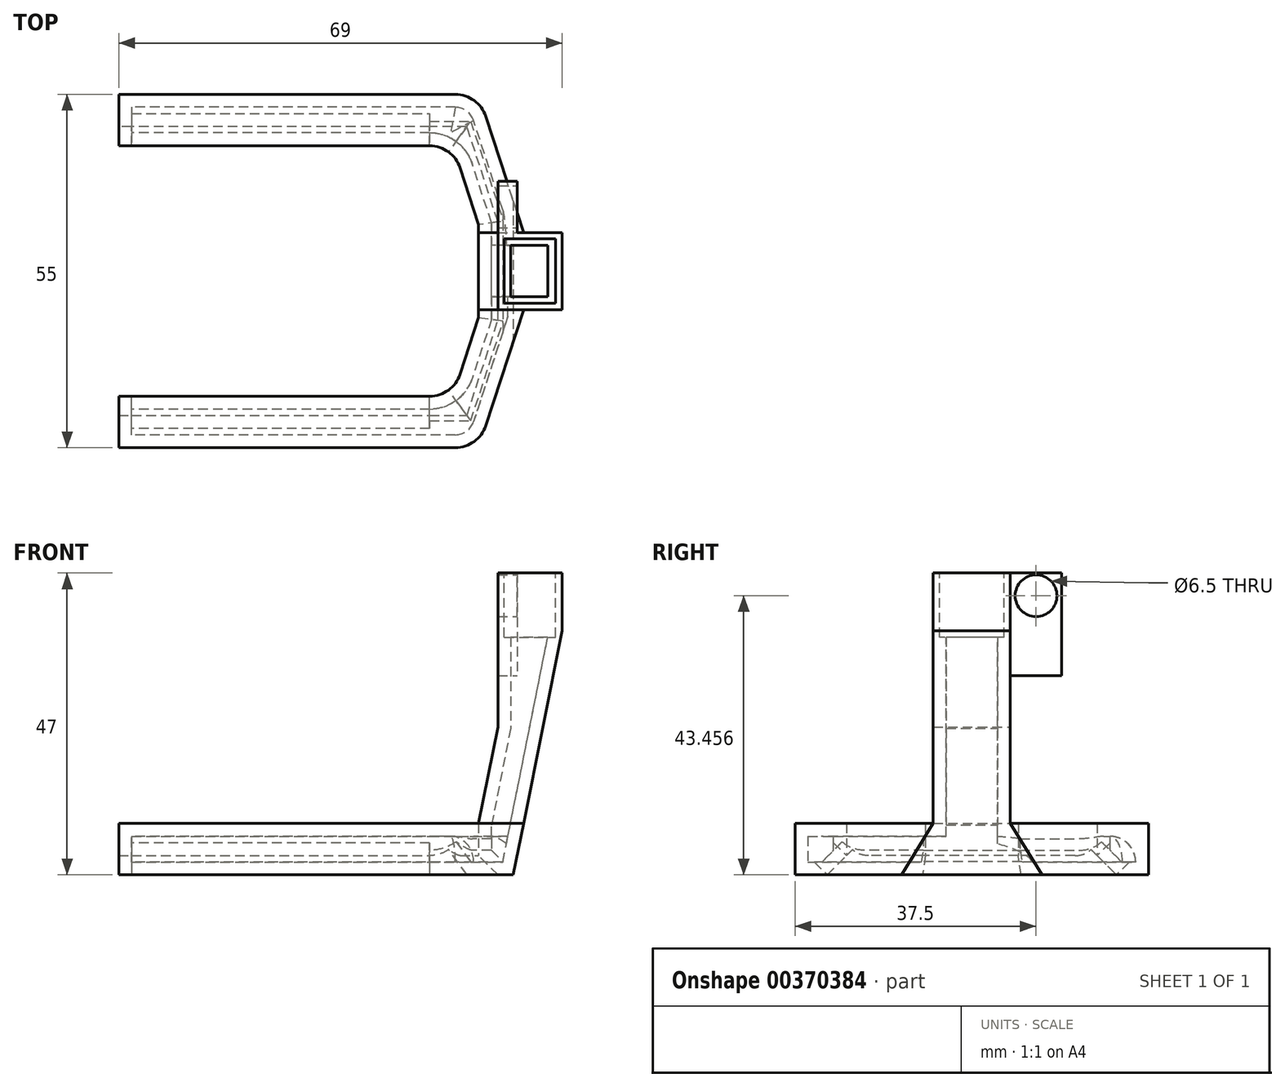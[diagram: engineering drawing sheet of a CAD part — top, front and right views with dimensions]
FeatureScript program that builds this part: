
annotation { "Feature Type Name" : "Feature", "Feature Type Description" : "" }
export const myFeature = defineFeature(function(context is Context, id is Id, definition is map)
    precondition{}
    {
        {
            var Q0;
            Q0=qCreatedBy(makeId("Top.planeOp"),FACE);
            var sketch = newSketch(context, id + "F0", { "sketchPlane" : qUnion([Q0])});
            skLineSegment(sketch, "E0", {"start": v(-26, 19.5) * mm, "end": v(26, 19.5) * mm});
            skLineSegment(sketch, "E1", {"start": v(26, 19.5) * mm, "end": v(30, 7.21) * mm});
            skLineSegment(sketch, "E2", {"start": v(30, 7.21) * mm, "end": v(30, 0) * mm});
            skLineSegment(sketch, "E3", {"start": v(43, 0) * mm, "end": v(43, 6) * mm});
            skLineSegment(sketch, "E4", {"start": v(43, 6) * mm, "end": v(37, 6) * mm});
            skLineSegment(sketch, "E5", {"start": v(37, 6) * mm, "end": v(30, 27.5) * mm});
            skLineSegment(sketch, "E6", {"start": v(30, 27.5) * mm, "end": v(-26, 27.5) * mm});
            skLineSegment(sketch, "E7", {"start": v(-26, 27.5) * mm, "end": v(-26, 19.5) * mm});
            skLineSegment(sketch, "E8.MirrorCS", {"start": v(43, 0) * mm, "end": v(43, -6) * mm});
            skLineSegment(sketch, "E9.MirrorCS", {"start": v(43, -6) * mm, "end": v(37, -6) * mm});
            skLineSegment(sketch, "E10.MirrorCS", {"start": v(37, -6) * mm, "end": v(30, -27.5) * mm});
            skLineSegment(sketch, "E11.MirrorCS", {"start": v(30, -7.21) * mm, "end": v(30, 0) * mm});
            skLineSegment(sketch, "E12.MirrorCS", {"start": v(26, -19.5) * mm, "end": v(30, -7.21) * mm});
            skLineSegment(sketch, "E13.MirrorCS", {"start": v(-26, -19.5) * mm, "end": v(26, -19.5) * mm});
            skLineSegment(sketch, "E14.MirrorCS", {"start": v(-26, -27.5) * mm, "end": v(-26, -19.5) * mm});
            skLineSegment(sketch, "E15.MirrorCS", {"start": v(30, -27.5) * mm, "end": v(-26, -27.5) * mm});
            skSolve(sketch);
        }
        {
            var Q0;
            Q0 = qSketchRegion(id + "F0", true);
            extrude(context, id + "F1", {"entities" : qUnion([Q0]), "depth" : 8 * mm, "offsetDistance" : 25 * mm});
        }
        {
            var Q0;
            Q0=makeQuery(id+"F1.opExtrude","CAP_EDGE",EDGE,{"disambiguationData":[OSD([sQuery(id+"F0.wireOp",EDGE,"E13.MirrorCS")])],"isStart":true});
            var Q1;
            Q1=makeQuery(id+"F1.opExtrude","CAP_EDGE",EDGE,{"disambiguationData":[OSD([sQuery(id+"F0.wireOp",EDGE,"E0")])],"isStart":true});
            var Q2;
            Q2=makeQuery(id+"F1.opExtrude","CAP_EDGE",EDGE,{"disambiguationData":[OSD([sQuery(id+"F0.wireOp",EDGE,"E1")])],"isStart":true});
            var Q3;
            Q3=makeQuery(id+"F1.opExtrude","CAP_EDGE",EDGE,{"disambiguationData":[OSD([sQuery(id+"F0.wireOp",EDGE,"E2"),sQuery(id+"F0.wireOp",EDGE,"E11.MirrorCS")])],"isStart":true});
            var Q4;
            Q4=makeQuery(id+"F1.opExtrude","CAP_EDGE",EDGE,{"disambiguationData":[OSD([sQuery(id+"F0.wireOp",EDGE,"E12.MirrorCS")])],"isStart":true});
            chamfer(context, id + "F2", {"entities" : qUnion([Q0, Q1, Q2, Q3, Q4]), "width" : 3 * mm, "tangentPropagation" : true});
        }
        {
            var Q0;
            Q0=qCreatedBy(makeId("Front.planeOp"),FACE);
            var sketch = newSketch(context, id + "F3", { "sketchPlane" : qUnion([Q0])});
            skLineSegment(sketch, "E16", {"start": v(43, 8) * mm, "end": v(43, 47) * mm});
            skLineSegment(sketch, "E17", {"start": v(43, 47) * mm, "end": v(33, 47) * mm});
            skLineSegment(sketch, "E18", {"start": v(33, 47) * mm, "end": v(33, 23) * mm});
            skLineSegment(sketch, "E19", {"start": v(33, 23) * mm, "end": v(30, 8) * mm});
            skLineSegment(sketch, "E20", {"start": v(30, 8) * mm, "end": v(43, 8) * mm});
            skSolve(sketch);
        }
        {
            var Q0;
            Q0=makeQuery(id+"F3.imprint","IMPRINT",FACE,{"disambiguationData":[TD([[makeQuery(id+"F3.imprint","IMPRINT",EDGE,{"derivedFrom":sQuery(id+"F3.wireOp",EDGE,"E16")}),1.0]])]});
            extrude(context, id + "F4", {"entities" : qUnion([Q0]), "operationType" : NewBodyOperationType.ADD, "endBound" : BoundingType.SYMMETRIC, "depth" : 12 * mm, "offsetDistance" : 25 * mm});
        }
        {
            var Q0;
            Q0=qCreatedBy(makeId("Front.planeOp"),FACE);
            var sketch = newSketch(context, id + "F5", { "sketchPlane" : qUnion([Q0])});
            skLineSegment(sketch, "E21", {"start": v(35.4, 0) * mm, "end": v(43, 38) * mm});
            skLineSegment(sketch, "E22", {"start": v(43, 38) * mm, "end": v(43, 0) * mm});
            skLineSegment(sketch, "E23", {"start": v(43, 0) * mm, "end": v(35.4, 0) * mm});
            skSolve(sketch);
        }
        {
            var Q0;
            Q0 = qSketchRegion(id + "F5", true);
            extrude(context, id + "F6", {"entities" : qUnion([Q0]), "operationType" : NewBodyOperationType.REMOVE, "endBound" : BoundingType.SYMMETRIC, "oppositeDirection" : true, "depth" : 50 * mm, "offsetDistance" : 25 * mm});
        }
        {
            var Q0;
            Q0=makeQuery(id+"F1.opExtrude","SWEPT_EDGE",EDGE,{"disambiguationData":[OSD([sQuery(id+"F0.wireOp",EDGE,"E5"),sQuery(id+"F0.wireOp",EDGE,"E6")])]});
            var Q1;
            Q1=makeQuery(id+"F1.opExtrude","SWEPT_EDGE",EDGE,{"disambiguationData":[OSD([sQuery(id+"F0.wireOp",EDGE,"E10.MirrorCS"),sQuery(id+"F0.wireOp",EDGE,"E15.MirrorCS")])]});
            var Q2;
            Q2=makeQuery(id+"F1.opExtrude","SWEPT_EDGE",EDGE,{"disambiguationData":[OSD([sQuery(id+"F0.wireOp",EDGE,"E0"),sQuery(id+"F0.wireOp",EDGE,"E1")])]});
            var Q3;
            Q3=makeQuery(id+"F1.opExtrude","SWEPT_EDGE",EDGE,{"disambiguationData":[OSD([sQuery(id+"F0.wireOp",EDGE,"E12.MirrorCS"),sQuery(id+"F0.wireOp",EDGE,"E13.MirrorCS")])]});
            fillet(context, id + "F7", {"entities" : qUnion([Q0, Q1, Q2, Q3]), "radius" : 5 * mm, "tangentPropagation" : true, "allowEdgeOverflow" : false});
        }
        {
            var Q0;
            Q0=makeQuery(id+"F4.opExtrude","SWEPT_FACE",FACE,{"disambiguationData":[OSD([sQuery(id+"F3.wireOp",EDGE,"E17")])]});
            shell(context, id + "F8", {"entities" : qUnion([Q0]), "thickness" : 2 * mm});
        }
        {
            var Q0;
            Q0=makeQuery(id+"F2.opChamfer","BLEND_FACE",FACE,{"disambiguationData":[OSD([sQuery(id+"F0.wireOp",EDGE,"E0")])]});
            var sketch = newSketch(context, id + "F9", { "sketchPlane" : qUnion([Q0])});
            skLineSegment(sketch, "E24.bottom", {"start": v(-24, -11.67) * mm, "end": v(22.37, -11.67) * mm});
            skLineSegment(sketch, "E24.top", {"start": v(-24, -15.9) * mm, "end": v(22.37, -15.9) * mm});
            skLineSegment(sketch, "E24.left", {"start": v(-24, -11.67) * mm, "end": v(-24, -15.9) * mm});
            skLineSegment(sketch, "E24.right", {"start": v(22.37, -11.67) * mm, "end": v(22.37, -15.9) * mm});
            skSolve(sketch);
        }
        {
            var Q0;
            {var subQ0=sQuery(id+"F0.wireOp",EDGE,"E6");Q0=makeQuery(id+"F8.opShell","OFFSET_EDGE",EDGE,{"disambiguationData":[OSD([subQ0]),TDD([makeQuery(id+"F1.opExtrude","CAP_EDGE",EDGE,{"disambiguationData":[OSD([subQ0])],"isStart":false})])]});}
            fillet(context, id + "F10", {"entities" : qUnion([Q0]), "radius" : 4 * mm, "tangentPropagation" : true, "allowEdgeOverflow" : false});
        }
        {
            var Q0;
            Q0=makeQuery(id+"F2.opChamfer","BLEND_FACE",FACE,{"disambiguationData":[OSD([sQuery(id+"F0.wireOp",EDGE,"E13.MirrorCS")])]});
            var sketch = newSketch(context, id + "F11", { "sketchPlane" : qUnion([Q0])});
            skLineSegment(sketch, "E25.bottom", {"start": v(-22.37, -11.67) * mm, "end": v(24, -11.67) * mm});
            skLineSegment(sketch, "E25.top", {"start": v(-22.37, -15.9) * mm, "end": v(24, -15.9) * mm});
            skLineSegment(sketch, "E25.left", {"start": v(24, -15.9) * mm, "end": v(24, -11.67) * mm});
            skLineSegment(sketch, "E25.right", {"start": v(-22.37, -15.9) * mm, "end": v(-22.37, -11.67) * mm});
            skSolve(sketch);
        }
        {
            var Q0;
            Q0=makeQuery(id+"F11.imprint","IMPRINT",FACE,{"disambiguationData":[TD([[makeQuery(id+"F11.imprint","IMPRINT",EDGE,{"derivedFrom":sQuery(id+"F11.wireOp",EDGE,"E25.bottom")}),-1.0]])]});
            extrude(context, id + "F12", {"entities" : qUnion([Q0]), "operationType" : NewBodyOperationType.REMOVE, "oppositeDirection" : true, "depth" : 3 * mm, "offsetDistance" : 25 * mm});
        }
        {
            var Q0;
            Q0 = qSketchRegion(id + "F9", true);
            extrude(context, id + "F13", {"entities" : qUnion([Q0]), "operationType" : NewBodyOperationType.REMOVE, "oppositeDirection" : true, "depth" : 3 * mm, "offsetDistance" : 25 * mm});
        }
        {
            var Q0;
            Q0=makeQuery(id+"F4.opExtrude","SWEPT_FACE",FACE,{"disambiguationData":[OSD([sQuery(id+"F3.wireOp",EDGE,"E17")])]});
            var sketch = newSketch(context, id + "F14", { "sketchPlane" : qUnion([Q0])});
            skLineSegment(sketch, "E26.bottom", {"start": v(34, 5) * mm, "end": v(42, 5) * mm});
            skLineSegment(sketch, "E26.top", {"start": v(34, -5) * mm, "end": v(42, -5) * mm});
            skLineSegment(sketch, "E26.left", {"start": v(34, 5) * mm, "end": v(34, -5) * mm});
            skLineSegment(sketch, "E26.right", {"start": v(42, 5) * mm, "end": v(42, -5) * mm});
            skSolve(sketch);
        }
        {
            var Q0;
            Q0=makeQuery(id+"F14.imprint","IMPRINT",FACE,{"disambiguationData":[TD([[makeQuery(id+"F14.imprint","IMPRINT",EDGE,{"derivedFrom":sQuery(id+"F14.wireOp",EDGE,"E26.bottom")}),-1.0]])]});
            var Q1;
            {var subQ0=sQuery(id+"F3.wireOp",EDGE,"E17");Q1=makeQuery(id+"F14.imprint","IMPRINT",FACE,{"disambiguationData":[TD([[makeQuery(id+"F14.imprint","IMPRINT",EDGE,{"derivedFrom":makeQuery(id+"F8.opShell","OFFSET_EDGE",EDGE,{"disambiguationData":[OSD([subQ0]),TDD([makeQuery(id+"F4.opExtrude","CAP_EDGE",EDGE,{"disambiguationData":[OSD([subQ0])],"isStart":true})])]})}),1.0]])]});}
            extrude(context, id + "F15", {"entities" : qUnion([Q0, Q1]), "operationType" : NewBodyOperationType.REMOVE, "oppositeDirection" : true, "depth" : 10 * mm, "offsetDistance" : 25 * mm});
        }
        {
            var Q0;
            Q0=makeQuery(id+"F4.boolean.opBoolean","MERGE",FACE,{"derivedFrom":[makeQuery(id+"F1.opExtrude","SWEPT_FACE",FACE,{"disambiguationData":[OSD([sQuery(id+"F0.wireOp",EDGE,"E4")])]}),makeQuery(id+"F4.opExtrude","CAP_FACE",FACE,{"disambiguationData":[OSD([sQuery(id+"F3.wireOp",EDGE,"E16"),sQuery(id+"F3.wireOp",EDGE,"E17"),sQuery(id+"F3.wireOp",EDGE,"E18"),sQuery(id+"F3.wireOp",EDGE,"E19"),sQuery(id+"F3.wireOp",EDGE,"E20")])],"isStart":true})]});
            var sketch = newSketch(context, id + "F16", { "sketchPlane" : qUnion([Q0])});
            skLineSegment(sketch, "E27.bottom", {"start": v(-33, 47) * mm, "end": v(-36, 47) * mm});
            skLineSegment(sketch, "E27.top", {"start": v(-33, 31) * mm, "end": v(-36, 31) * mm});
            skLineSegment(sketch, "E27.left", {"start": v(-33, 47) * mm, "end": v(-33, 31) * mm});
            skLineSegment(sketch, "E27.right", {"start": v(-36, 47) * mm, "end": v(-36, 31) * mm});
            skSolve(sketch);
        }
        {
            var Q0;
            Q0 = qSketchRegion(id + "F16", true);
            extrude(context, id + "F17", {"entities" : qUnion([Q0]), "operationType" : NewBodyOperationType.ADD, "depth" : 8 * mm, "offsetDistance" : 25 * mm});
        }
        {
            var Q0;
            Q0=makeQuery(id+"F17.opExtrude","SWEPT_FACE",FACE,{"disambiguationData":[OSD([sQuery(id+"F16.wireOp",EDGE,"E27.right")])]});
            var sketch = newSketch(context, id + "F18", { "sketchPlane" : qUnion([Q0])});
            skPoint(sketch, "E28", {"position": v(10, 43.46) * mm});
            skPoint(sketch, "E29", {"position": v(10, 35.35) * mm});
            skLineSegment(sketch, "E30", {"start": v(10, 47) * mm, "end": v(10, 31) * mm, "construction": true});
            skSolve(sketch);
        }
        {
            var Q0;
            Q0=sQuery(id+"F18.wireOp",VERTEX,"E28");
            var Q1;
            Q1=makeQuery(id+"F1.opExtrude","SWEPT_BODY",BODY,{"disambiguationData":[OSD([sQuery(id+"F0.wireOp",EDGE,"E0"),sQuery(id+"F0.wireOp",EDGE,"E1"),sQuery(id+"F0.wireOp",EDGE,"E2"),sQuery(id+"F0.wireOp",EDGE,"E3"),sQuery(id+"F0.wireOp",EDGE,"E4"),sQuery(id+"F0.wireOp",EDGE,"E5"),sQuery(id+"F0.wireOp",EDGE,"E6"),sQuery(id+"F0.wireOp",EDGE,"E7"),sQuery(id+"F0.wireOp",EDGE,"E8.MirrorCS"),sQuery(id+"F0.wireOp",EDGE,"E9.MirrorCS"),sQuery(id+"F0.wireOp",EDGE,"E10.MirrorCS"),sQuery(id+"F0.wireOp",EDGE,"E11.MirrorCS"),sQuery(id+"F0.wireOp",EDGE,"E12.MirrorCS"),sQuery(id+"F0.wireOp",EDGE,"E13.MirrorCS"),sQuery(id+"F0.wireOp",EDGE,"E14.MirrorCS"),sQuery(id+"F0.wireOp",EDGE,"E15.MirrorCS")])]});
            hole(context, id + "F19", {"style" : HoleStyle.C_BORE, "endStyle" : HoleEndStyle.THROUGH, "standardTappedOrClearance" : lookupTablePath({ "standard" : "ISO", "fit" : "Normal", "size" : "M3", "type" : "Clearance" }), "standardBlindInLast" : lookupTablePath({ "fit" : "Standard", "standard" : "ISO", "size" : "M3", "type" : "Clearance" }), "holeDiameter" : 3.3 * mm, "cBoreDiameter" : 6.5 * mm, "cBoreDepth" : 3 * mm, "majorDiameter" : 5 * mm, "isTappedThrough" : true, "tappedDepth" : 12 * mm, "tapClearance" : 3, "locations" : qUnion([Q0]), "scope" : qUnion([Q1])});
        }
    });
